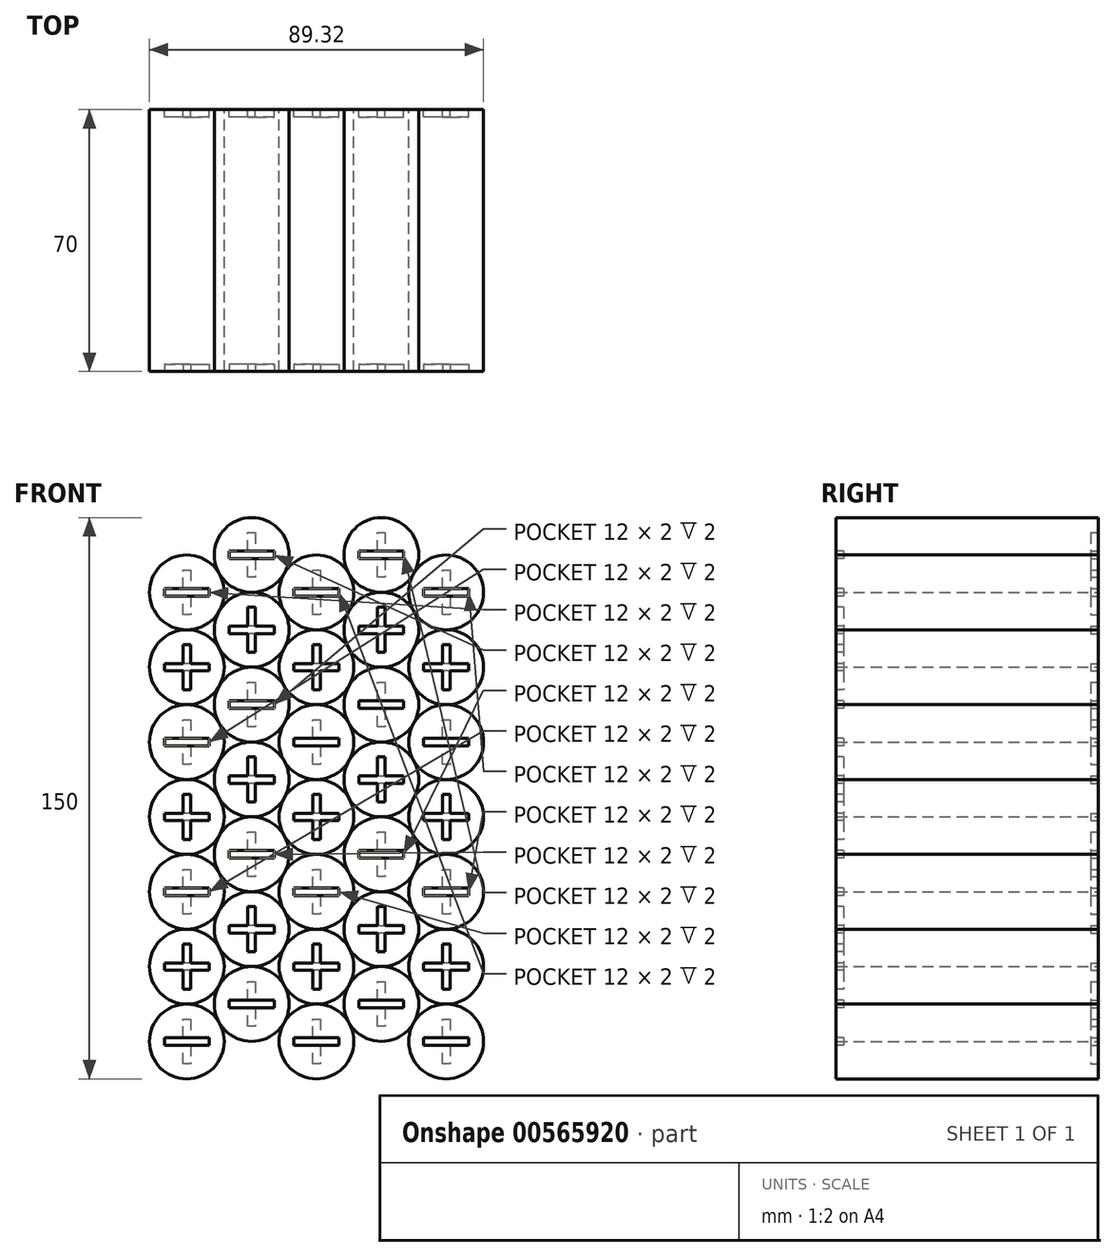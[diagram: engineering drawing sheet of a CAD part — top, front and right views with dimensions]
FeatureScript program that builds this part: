
annotation { "Feature Type Name" : "Feature", "Feature Type Description" : "" }
export const myFeature = defineFeature(function(context is Context, id is Id, definition is map)
    precondition{}
    {
        {
            var Q0;
            Q0=qCreatedBy(makeId("Front.planeOp"),FACE);
            var sketch = newSketch(context, id + "F0", { "sketchPlane" : qUnion([Q0])});
            skCircle(sketch, "E0", {"center": v(10, 10) * mm, "radius": 10 * mm});
            skCircle(sketch, "E1", {"center": v(27.33, 20) * mm, "radius": 10 * mm});
            skCircle(sketch, "E2", {"center": v(44.66, 10) * mm, "radius": 10 * mm});
            skCircle(sketch, "E3", {"center": v(62, 20) * mm, "radius": 10 * mm});
            skCircle(sketch, "E4", {"center": v(79.32, 10) * mm, "radius": 10 * mm});
            skCircle(sketch, "E5", {"center": v(10, 30) * mm, "radius": 10 * mm});
            skCircle(sketch, "E6", {"center": v(27.33, 40) * mm, "radius": 10 * mm});
            skCircle(sketch, "E7", {"center": v(44.66, 30) * mm, "radius": 10 * mm});
            skCircle(sketch, "E8", {"center": v(62, 40) * mm, "radius": 10 * mm});
            skCircle(sketch, "E9", {"center": v(79.32, 30) * mm, "radius": 10 * mm});
            skCircle(sketch, "E10", {"center": v(10, 50) * mm, "radius": 10 * mm});
            skCircle(sketch, "E11", {"center": v(27.33, 60) * mm, "radius": 10 * mm});
            skCircle(sketch, "E12", {"center": v(44.66, 50) * mm, "radius": 10 * mm});
            skCircle(sketch, "E13", {"center": v(62, 60) * mm, "radius": 10 * mm});
            skCircle(sketch, "E14", {"center": v(79.32, 50) * mm, "radius": 10 * mm});
            skCircle(sketch, "E15", {"center": v(10, 70) * mm, "radius": 10 * mm});
            skCircle(sketch, "E16", {"center": v(27.33, 80) * mm, "radius": 10 * mm});
            skCircle(sketch, "E17", {"center": v(44.66, 70) * mm, "radius": 10 * mm});
            skCircle(sketch, "E18", {"center": v(62, 80) * mm, "radius": 10 * mm});
            skCircle(sketch, "E19", {"center": v(79.32, 70) * mm, "radius": 10 * mm});
            skCircle(sketch, "E20", {"center": v(10, 90) * mm, "radius": 10 * mm});
            skCircle(sketch, "E21", {"center": v(27.33, 100) * mm, "radius": 10 * mm});
            skCircle(sketch, "E22", {"center": v(44.66, 90) * mm, "radius": 10 * mm});
            skCircle(sketch, "E23", {"center": v(62, 100) * mm, "radius": 10 * mm});
            skCircle(sketch, "E24", {"center": v(79.32, 90) * mm, "radius": 10 * mm});
            skCircle(sketch, "E25", {"center": v(10, 110) * mm, "radius": 10 * mm});
            skCircle(sketch, "E26", {"center": v(27.33, 120) * mm, "radius": 10 * mm});
            skCircle(sketch, "E27", {"center": v(44.66, 110) * mm, "radius": 10 * mm});
            skCircle(sketch, "E28", {"center": v(62, 120) * mm, "radius": 10 * mm});
            skCircle(sketch, "E29", {"center": v(79.32, 110) * mm, "radius": 10 * mm});
            skCircle(sketch, "E30", {"center": v(10, 130) * mm, "radius": 10 * mm});
            skCircle(sketch, "E31", {"center": v(27.33, 140) * mm, "radius": 10 * mm});
            skCircle(sketch, "E32", {"center": v(44.66, 130) * mm, "radius": 10 * mm});
            skCircle(sketch, "E33", {"center": v(62, 140) * mm, "radius": 10 * mm});
            skCircle(sketch, "E34", {"center": v(79.32, 130) * mm, "radius": 10 * mm});
            skSolve(sketch);
        }
        {
            var Q0;
            Q0=qSketchRegion(id+"F0",true);
            extrude(context, id + "F1", {"entities" : qUnion([Q0]), "depth" : 70 * mm, "offsetDistance" : 25 * mm});
        }
        {
            var Q0;
            Q0=makeQuery(id+"F1.opExtrude","CAP_FACE",FACE,{"disambiguationData":[OSD([sQuery(id+"F0.wireOp",EDGE,"E34")])],"isStart":true});
            var sketch = newSketch(context, id + "F2", { "sketchPlane" : qUnion([Q0])});
            skLineSegment(sketch, "E35", {"start": v(-80.32, 16) * mm, "end": v(-80.32, 11) * mm});
            skLineSegment(sketch, "E36", {"start": v(-80.32, 11) * mm, "end": v(-85.32, 11) * mm});
            skLineSegment(sketch, "E37", {"start": v(-85.32, 11) * mm, "end": v(-85.32, 9) * mm});
            skLineSegment(sketch, "E38", {"start": v(-85.32, 9) * mm, "end": v(-80.32, 9) * mm});
            skLineSegment(sketch, "E39", {"start": v(-80.32, 9) * mm, "end": v(-80.32, 4) * mm});
            skLineSegment(sketch, "E40", {"start": v(-80.32, 4) * mm, "end": v(-78.32, 4) * mm});
            skLineSegment(sketch, "E41", {"start": v(-78.32, 4) * mm, "end": v(-78.32, 9) * mm});
            skLineSegment(sketch, "E42", {"start": v(-78.32, 9) * mm, "end": v(-73.32, 9) * mm});
            skLineSegment(sketch, "E43", {"start": v(-73.32, 9) * mm, "end": v(-73.32, 11) * mm});
            skLineSegment(sketch, "E44", {"start": v(-73.32, 11) * mm, "end": v(-78.32, 11) * mm});
            skLineSegment(sketch, "E45", {"start": v(-78.32, 11) * mm, "end": v(-78.32, 16) * mm});
            skLineSegment(sketch, "E46", {"start": v(-78.32, 16) * mm, "end": v(-80.32, 16) * mm});
            skLineSegment(sketch, "E47", {"start": v(-63, 26) * mm, "end": v(-63, 21) * mm});
            skLineSegment(sketch, "E48", {"start": v(-63, 21) * mm, "end": v(-68, 21) * mm});
            skLineSegment(sketch, "E49", {"start": v(-68, 21) * mm, "end": v(-68, 19) * mm});
            skLineSegment(sketch, "E50", {"start": v(-68, 19) * mm, "end": v(-63, 19) * mm});
            skLineSegment(sketch, "E51", {"start": v(-63, 19) * mm, "end": v(-63, 14) * mm});
            skLineSegment(sketch, "E52", {"start": v(-63, 14) * mm, "end": v(-60.99, 14) * mm});
            skLineSegment(sketch, "E53", {"start": v(-61, 14) * mm, "end": v(-61, 19) * mm});
            skLineSegment(sketch, "E54", {"start": v(-61, 19) * mm, "end": v(-55.99, 19) * mm});
            skLineSegment(sketch, "E55", {"start": v(-55.99, 19) * mm, "end": v(-55.99, 21) * mm});
            skLineSegment(sketch, "E56", {"start": v(-55.99, 21) * mm, "end": v(-61, 21) * mm});
            skLineSegment(sketch, "E57", {"start": v(-61, 21) * mm, "end": v(-61, 26) * mm});
            skLineSegment(sketch, "E58", {"start": v(-61, 26) * mm, "end": v(-63, 26) * mm});
            skLineSegment(sketch, "E59", {"start": v(-11, 16) * mm, "end": v(-11, 11) * mm});
            skLineSegment(sketch, "E60", {"start": v(-11, 11) * mm, "end": v(-16, 11) * mm});
            skLineSegment(sketch, "E61", {"start": v(-16, 11) * mm, "end": v(-16, 9) * mm});
            skLineSegment(sketch, "E62", {"start": v(-16, 9) * mm, "end": v(-11, 9) * mm});
            skLineSegment(sketch, "E63", {"start": v(-11, 9) * mm, "end": v(-11, 4) * mm});
            skLineSegment(sketch, "E64", {"start": v(-11, 4) * mm, "end": v(-9, 4) * mm});
            skLineSegment(sketch, "E65", {"start": v(-9, 4) * mm, "end": v(-9, 9) * mm});
            skLineSegment(sketch, "E66", {"start": v(-9, 9) * mm, "end": v(-4, 9) * mm});
            skLineSegment(sketch, "E67", {"start": v(-4, 9) * mm, "end": v(-4, 11) * mm});
            skLineSegment(sketch, "E68", {"start": v(-4, 11) * mm, "end": v(-9, 11) * mm});
            skLineSegment(sketch, "E69", {"start": v(-9, 11) * mm, "end": v(-9, 16) * mm});
            skLineSegment(sketch, "E70", {"start": v(-9, 16) * mm, "end": v(-11, 16) * mm});
            skLineSegment(sketch, "E71", {"start": v(-28.33, 26) * mm, "end": v(-28.33, 21) * mm});
            skLineSegment(sketch, "E72", {"start": v(-28.33, 21) * mm, "end": v(-33.33, 21) * mm});
            skLineSegment(sketch, "E73", {"start": v(-33.33, 21) * mm, "end": v(-33.33, 19) * mm});
            skLineSegment(sketch, "E74", {"start": v(-33.33, 19) * mm, "end": v(-28.33, 19) * mm});
            skLineSegment(sketch, "E75", {"start": v(-28.33, 19) * mm, "end": v(-28.33, 14) * mm});
            skLineSegment(sketch, "E76", {"start": v(-28.33, 14) * mm, "end": v(-26.33, 14) * mm});
            skLineSegment(sketch, "E77", {"start": v(-26.33, 14) * mm, "end": v(-26.33, 19) * mm});
            skLineSegment(sketch, "E78", {"start": v(-26.33, 19) * mm, "end": v(-21.33, 19) * mm});
            skLineSegment(sketch, "E79", {"start": v(-21.33, 19) * mm, "end": v(-21.33, 21) * mm});
            skLineSegment(sketch, "E80", {"start": v(-21.33, 21) * mm, "end": v(-26.33, 21) * mm});
            skLineSegment(sketch, "E81", {"start": v(-26.33, 21) * mm, "end": v(-26.33, 26) * mm});
            skLineSegment(sketch, "E82", {"start": v(-26.33, 26) * mm, "end": v(-28.33, 26) * mm});
            skLineSegment(sketch, "E83", {"start": v(-45.66, 16) * mm, "end": v(-45.66, 11) * mm});
            skLineSegment(sketch, "E84", {"start": v(-45.66, 11) * mm, "end": v(-50.66, 11) * mm});
            skLineSegment(sketch, "E85", {"start": v(-50.66, 11) * mm, "end": v(-50.66, 9) * mm});
            skLineSegment(sketch, "E86", {"start": v(-50.66, 9) * mm, "end": v(-45.66, 9) * mm});
            skLineSegment(sketch, "E87", {"start": v(-45.66, 9) * mm, "end": v(-45.66, 4) * mm});
            skLineSegment(sketch, "E88", {"start": v(-45.66, 4) * mm, "end": v(-43.66, 4) * mm});
            skLineSegment(sketch, "E89", {"start": v(-43.66, 4) * mm, "end": v(-43.66, 9) * mm});
            skLineSegment(sketch, "E90", {"start": v(-43.66, 9) * mm, "end": v(-38.66, 9) * mm});
            skLineSegment(sketch, "E91", {"start": v(-38.66, 9) * mm, "end": v(-38.66, 11) * mm});
            skLineSegment(sketch, "E92", {"start": v(-38.66, 11) * mm, "end": v(-43.66, 11) * mm});
            skLineSegment(sketch, "E93", {"start": v(-43.66, 11) * mm, "end": v(-43.66, 16) * mm});
            skLineSegment(sketch, "E94", {"start": v(-43.66, 16) * mm, "end": v(-45.66, 16) * mm});
            skLineSegment(sketch, "E95.bottom", {"start": v(-85.32, 31) * mm, "end": v(-73.32, 31) * mm});
            skLineSegment(sketch, "E95.top", {"start": v(-85.32, 29) * mm, "end": v(-73.32, 29) * mm});
            skLineSegment(sketch, "E95.left", {"start": v(-85.32, 31) * mm, "end": v(-85.32, 29) * mm});
            skLineSegment(sketch, "E95.right", {"start": v(-73.32, 31) * mm, "end": v(-73.32, 29) * mm});
            skLineSegment(sketch, "E96.bottom", {"start": v(-55.99, 41) * mm, "end": v(-68, 41) * mm});
            skLineSegment(sketch, "E96.top", {"start": v(-68, 39) * mm, "end": v(-55.99, 39) * mm});
            skLineSegment(sketch, "E96.left", {"start": v(-68, 41) * mm, "end": v(-68, 39) * mm});
            skLineSegment(sketch, "E96.right", {"start": v(-55.99, 41) * mm, "end": v(-55.99, 39) * mm});
            skLineSegment(sketch, "E97.bottom", {"start": v(-50.66, 31) * mm, "end": v(-38.66, 31) * mm});
            skLineSegment(sketch, "E97.top", {"start": v(-50.66, 29) * mm, "end": v(-38.66, 29) * mm});
            skLineSegment(sketch, "E97.left", {"start": v(-50.66, 31) * mm, "end": v(-50.66, 29) * mm});
            skLineSegment(sketch, "E97.right", {"start": v(-38.66, 31) * mm, "end": v(-38.66, 29) * mm});
            skLineSegment(sketch, "E98.bottom", {"start": v(-33.33, 41) * mm, "end": v(-21.33, 41) * mm});
            skLineSegment(sketch, "E98.top", {"start": v(-33.33, 39) * mm, "end": v(-21.33, 39) * mm});
            skLineSegment(sketch, "E98.left", {"start": v(-33.33, 41) * mm, "end": v(-33.33, 39) * mm});
            skLineSegment(sketch, "E98.right", {"start": v(-21.33, 41) * mm, "end": v(-21.33, 39) * mm});
            skLineSegment(sketch, "E99.bottom", {"start": v(-16, 31) * mm, "end": v(-4, 31) * mm});
            skLineSegment(sketch, "E99.top", {"start": v(-16, 29) * mm, "end": v(-4, 29) * mm});
            skLineSegment(sketch, "E99.left", {"start": v(-16, 31) * mm, "end": v(-16, 29) * mm});
            skLineSegment(sketch, "E99.right", {"start": v(-4, 31) * mm, "end": v(-4, 29) * mm});
            skLineSegment(sketch, "E100", {"start": v(-80.32, 56) * mm, "end": v(-80.32, 51) * mm});
            skLineSegment(sketch, "E101", {"start": v(-80.32, 51) * mm, "end": v(-85.32, 51) * mm});
            skLineSegment(sketch, "E102", {"start": v(-85.32, 51) * mm, "end": v(-85.32, 49) * mm});
            skLineSegment(sketch, "E103", {"start": v(-85.32, 49) * mm, "end": v(-80.32, 49) * mm});
            skLineSegment(sketch, "E104", {"start": v(-80.32, 49) * mm, "end": v(-80.32, 44) * mm});
            skLineSegment(sketch, "E105", {"start": v(-80.32, 44) * mm, "end": v(-78.32, 44) * mm});
            skLineSegment(sketch, "E106", {"start": v(-78.32, 44) * mm, "end": v(-78.32, 49) * mm});
            skLineSegment(sketch, "E107", {"start": v(-78.32, 49) * mm, "end": v(-73.32, 49) * mm});
            skLineSegment(sketch, "E108", {"start": v(-73.32, 49) * mm, "end": v(-73.32, 51) * mm});
            skLineSegment(sketch, "E109", {"start": v(-73.32, 51) * mm, "end": v(-78.32, 51) * mm});
            skLineSegment(sketch, "E110", {"start": v(-78.32, 51) * mm, "end": v(-78.32, 56) * mm});
            skLineSegment(sketch, "E111", {"start": v(-78.32, 56) * mm, "end": v(-80.32, 56) * mm});
            skLineSegment(sketch, "E112", {"start": v(-63, 66) * mm, "end": v(-63, 61) * mm});
            skLineSegment(sketch, "E113", {"start": v(-63, 61) * mm, "end": v(-68, 61) * mm});
            skLineSegment(sketch, "E114", {"start": v(-68, 61) * mm, "end": v(-68, 59) * mm});
            skLineSegment(sketch, "E115", {"start": v(-68, 59) * mm, "end": v(-63, 59) * mm});
            skLineSegment(sketch, "E116", {"start": v(-63, 59) * mm, "end": v(-63, 54) * mm});
            skLineSegment(sketch, "E117", {"start": v(-63, 54) * mm, "end": v(-61, 54) * mm});
            skLineSegment(sketch, "E118", {"start": v(-61, 54) * mm, "end": v(-61, 59) * mm});
            skLineSegment(sketch, "E119", {"start": v(-61, 59) * mm, "end": v(-55.99, 59) * mm});
            skLineSegment(sketch, "E120", {"start": v(-55.99, 59) * mm, "end": v(-55.99, 61) * mm});
            skLineSegment(sketch, "E121", {"start": v(-55.99, 61) * mm, "end": v(-61, 61) * mm});
            skLineSegment(sketch, "E122", {"start": v(-61, 61) * mm, "end": v(-61, 66) * mm});
            skLineSegment(sketch, "E123", {"start": v(-61, 66) * mm, "end": v(-62.99, 66) * mm});
            skLineSegment(sketch, "E124", {"start": v(-11, 56) * mm, "end": v(-11, 51) * mm});
            skLineSegment(sketch, "E125", {"start": v(-11, 51) * mm, "end": v(-16, 51) * mm});
            skLineSegment(sketch, "E126", {"start": v(-16, 51) * mm, "end": v(-16, 49) * mm});
            skLineSegment(sketch, "E127", {"start": v(-16, 49) * mm, "end": v(-11, 49) * mm});
            skLineSegment(sketch, "E128", {"start": v(-11, 49) * mm, "end": v(-11, 44) * mm});
            skLineSegment(sketch, "E129", {"start": v(-11, 44) * mm, "end": v(-9, 44) * mm});
            skLineSegment(sketch, "E130", {"start": v(-9, 44) * mm, "end": v(-9, 49) * mm});
            skLineSegment(sketch, "E131", {"start": v(-9, 49) * mm, "end": v(-4, 49) * mm});
            skLineSegment(sketch, "E132", {"start": v(-4, 49) * mm, "end": v(-4, 51) * mm});
            skLineSegment(sketch, "E133", {"start": v(-4, 51) * mm, "end": v(-9, 51) * mm});
            skLineSegment(sketch, "E134", {"start": v(-9, 51) * mm, "end": v(-9, 56) * mm});
            skLineSegment(sketch, "E135", {"start": v(-9, 56) * mm, "end": v(-11, 56) * mm});
            skLineSegment(sketch, "E136", {"start": v(-28.33, 66) * mm, "end": v(-28.33, 61) * mm});
            skLineSegment(sketch, "E137", {"start": v(-28.33, 61) * mm, "end": v(-33.33, 61) * mm});
            skLineSegment(sketch, "E138", {"start": v(-33.33, 61) * mm, "end": v(-33.33, 59) * mm});
            skLineSegment(sketch, "E139", {"start": v(-33.33, 59) * mm, "end": v(-28.33, 59) * mm});
            skLineSegment(sketch, "E140", {"start": v(-28.33, 59) * mm, "end": v(-28.33, 54) * mm});
            skLineSegment(sketch, "E141", {"start": v(-28.33, 54) * mm, "end": v(-26.33, 54) * mm});
            skLineSegment(sketch, "E142", {"start": v(-26.33, 54) * mm, "end": v(-26.33, 59) * mm});
            skLineSegment(sketch, "E143", {"start": v(-26.33, 59) * mm, "end": v(-21.33, 59) * mm});
            skLineSegment(sketch, "E144", {"start": v(-21.33, 59) * mm, "end": v(-21.33, 61) * mm});
            skLineSegment(sketch, "E145", {"start": v(-21.33, 61) * mm, "end": v(-26.33, 61) * mm});
            skLineSegment(sketch, "E146", {"start": v(-26.33, 61) * mm, "end": v(-26.33, 66) * mm});
            skLineSegment(sketch, "E147", {"start": v(-26.33, 66) * mm, "end": v(-28.33, 66) * mm});
            skLineSegment(sketch, "E148", {"start": v(-45.66, 56) * mm, "end": v(-45.66, 51) * mm});
            skLineSegment(sketch, "E149", {"start": v(-45.66, 51) * mm, "end": v(-50.66, 51) * mm});
            skLineSegment(sketch, "E150", {"start": v(-50.66, 51) * mm, "end": v(-50.66, 49) * mm});
            skLineSegment(sketch, "E151", {"start": v(-50.66, 49) * mm, "end": v(-45.66, 49) * mm});
            skLineSegment(sketch, "E152", {"start": v(-45.66, 49) * mm, "end": v(-45.66, 44) * mm});
            skLineSegment(sketch, "E153", {"start": v(-45.66, 44) * mm, "end": v(-43.66, 44) * mm});
            skLineSegment(sketch, "E154", {"start": v(-43.66, 44) * mm, "end": v(-43.66, 49) * mm});
            skLineSegment(sketch, "E155", {"start": v(-43.66, 49) * mm, "end": v(-38.66, 49) * mm});
            skLineSegment(sketch, "E156", {"start": v(-38.66, 49) * mm, "end": v(-38.66, 51) * mm});
            skLineSegment(sketch, "E157", {"start": v(-38.66, 51) * mm, "end": v(-43.66, 51) * mm});
            skLineSegment(sketch, "E158", {"start": v(-43.66, 51) * mm, "end": v(-43.66, 56) * mm});
            skLineSegment(sketch, "E159", {"start": v(-43.66, 56) * mm, "end": v(-45.66, 56) * mm});
            skLineSegment(sketch, "E160.bottom", {"start": v(-85.32, 71) * mm, "end": v(-73.32, 71) * mm});
            skLineSegment(sketch, "E160.top", {"start": v(-85.32, 69) * mm, "end": v(-73.32, 69) * mm});
            skLineSegment(sketch, "E160.left", {"start": v(-85.32, 71) * mm, "end": v(-85.32, 69) * mm});
            skLineSegment(sketch, "E160.right", {"start": v(-73.32, 71) * mm, "end": v(-73.32, 69) * mm});
            skLineSegment(sketch, "E161.bottom", {"start": v(-55.99, 81) * mm, "end": v(-68, 81) * mm});
            skLineSegment(sketch, "E161.top", {"start": v(-68, 79) * mm, "end": v(-55.99, 79) * mm});
            skLineSegment(sketch, "E161.left", {"start": v(-68, 81) * mm, "end": v(-68, 79) * mm});
            skLineSegment(sketch, "E161.right", {"start": v(-55.99, 81) * mm, "end": v(-55.99, 79) * mm});
            skLineSegment(sketch, "E162.bottom", {"start": v(-50.66, 71) * mm, "end": v(-38.66, 71) * mm});
            skLineSegment(sketch, "E162.top", {"start": v(-50.66, 69) * mm, "end": v(-38.66, 69) * mm});
            skLineSegment(sketch, "E162.left", {"start": v(-50.66, 71) * mm, "end": v(-50.66, 69) * mm});
            skLineSegment(sketch, "E162.right", {"start": v(-38.66, 71) * mm, "end": v(-38.66, 69) * mm});
            skLineSegment(sketch, "E163.bottom", {"start": v(-33.33, 81) * mm, "end": v(-21.33, 81) * mm});
            skLineSegment(sketch, "E163.top", {"start": v(-33.33, 79) * mm, "end": v(-21.33, 79) * mm});
            skLineSegment(sketch, "E163.left", {"start": v(-33.33, 81) * mm, "end": v(-33.33, 79) * mm});
            skLineSegment(sketch, "E163.right", {"start": v(-21.33, 81) * mm, "end": v(-21.33, 79) * mm});
            skLineSegment(sketch, "E164.bottom", {"start": v(-16, 71) * mm, "end": v(-4, 71) * mm});
            skLineSegment(sketch, "E164.top", {"start": v(-16, 69) * mm, "end": v(-4, 69) * mm});
            skLineSegment(sketch, "E164.left", {"start": v(-16, 71) * mm, "end": v(-16, 69) * mm});
            skLineSegment(sketch, "E164.right", {"start": v(-4, 71) * mm, "end": v(-4, 69) * mm});
            skLineSegment(sketch, "E165", {"start": v(-80.32, 96) * mm, "end": v(-80.32, 91) * mm});
            skLineSegment(sketch, "E166", {"start": v(-80.32, 91) * mm, "end": v(-85.32, 91) * mm});
            skLineSegment(sketch, "E167", {"start": v(-85.32, 91) * mm, "end": v(-85.32, 89) * mm});
            skLineSegment(sketch, "E168", {"start": v(-85.32, 89) * mm, "end": v(-80.32, 89) * mm});
            skLineSegment(sketch, "E169", {"start": v(-80.32, 89) * mm, "end": v(-80.32, 84) * mm});
            skLineSegment(sketch, "E170", {"start": v(-80.32, 84) * mm, "end": v(-78.32, 84) * mm});
            skLineSegment(sketch, "E171", {"start": v(-78.32, 84) * mm, "end": v(-78.32, 89) * mm});
            skLineSegment(sketch, "E172", {"start": v(-78.32, 89) * mm, "end": v(-73.32, 89) * mm});
            skLineSegment(sketch, "E173", {"start": v(-73.32, 89) * mm, "end": v(-73.32, 91) * mm});
            skLineSegment(sketch, "E174", {"start": v(-73.32, 91) * mm, "end": v(-78.32, 91) * mm});
            skLineSegment(sketch, "E175", {"start": v(-78.32, 91) * mm, "end": v(-78.32, 96) * mm});
            skLineSegment(sketch, "E176", {"start": v(-78.32, 96) * mm, "end": v(-80.32, 96) * mm});
            skLineSegment(sketch, "E177", {"start": v(-63, 106) * mm, "end": v(-63, 101) * mm});
            skLineSegment(sketch, "E178", {"start": v(-63, 101) * mm, "end": v(-68, 101) * mm});
            skLineSegment(sketch, "E179", {"start": v(-68, 101) * mm, "end": v(-68, 99) * mm});
            skLineSegment(sketch, "E180", {"start": v(-68, 99) * mm, "end": v(-63, 99) * mm});
            skLineSegment(sketch, "E181", {"start": v(-63, 99) * mm, "end": v(-63, 94) * mm});
            skLineSegment(sketch, "E182", {"start": v(-63, 94) * mm, "end": v(-61, 94) * mm});
            skLineSegment(sketch, "E183", {"start": v(-61, 94) * mm, "end": v(-61, 99) * mm});
            skLineSegment(sketch, "E184", {"start": v(-61, 99) * mm, "end": v(-56, 99) * mm});
            skLineSegment(sketch, "E185", {"start": v(-56, 99) * mm, "end": v(-56, 101) * mm});
            skLineSegment(sketch, "E186", {"start": v(-56, 101) * mm, "end": v(-61, 101) * mm});
            skLineSegment(sketch, "E187", {"start": v(-61, 101) * mm, "end": v(-61, 106) * mm});
            skLineSegment(sketch, "E188", {"start": v(-61, 106) * mm, "end": v(-62.99, 106) * mm});
            skLineSegment(sketch, "E189", {"start": v(-11, 96) * mm, "end": v(-11, 91) * mm});
            skLineSegment(sketch, "E190", {"start": v(-11, 91) * mm, "end": v(-16, 91) * mm});
            skLineSegment(sketch, "E191", {"start": v(-16, 91) * mm, "end": v(-16, 89) * mm});
            skLineSegment(sketch, "E192", {"start": v(-16, 89) * mm, "end": v(-11, 89) * mm});
            skLineSegment(sketch, "E193", {"start": v(-11, 89) * mm, "end": v(-11, 84) * mm});
            skLineSegment(sketch, "E194", {"start": v(-11, 84) * mm, "end": v(-9, 84) * mm});
            skLineSegment(sketch, "E195", {"start": v(-9, 84) * mm, "end": v(-9, 89) * mm});
            skLineSegment(sketch, "E196", {"start": v(-9, 89) * mm, "end": v(-4, 89) * mm});
            skLineSegment(sketch, "E197", {"start": v(-4, 89) * mm, "end": v(-4, 91) * mm});
            skLineSegment(sketch, "E198", {"start": v(-4, 91) * mm, "end": v(-9, 91) * mm});
            skLineSegment(sketch, "E199", {"start": v(-9, 91) * mm, "end": v(-9, 96) * mm});
            skLineSegment(sketch, "E200", {"start": v(-9, 96) * mm, "end": v(-11, 96) * mm});
            skLineSegment(sketch, "E201", {"start": v(-28.33, 106) * mm, "end": v(-28.33, 101) * mm});
            skLineSegment(sketch, "E202", {"start": v(-28.33, 101) * mm, "end": v(-33.33, 101) * mm});
            skLineSegment(sketch, "E203", {"start": v(-33.33, 101) * mm, "end": v(-33.33, 99) * mm});
            skLineSegment(sketch, "E204", {"start": v(-33.33, 99) * mm, "end": v(-28.33, 99) * mm});
            skLineSegment(sketch, "E205", {"start": v(-28.33, 99) * mm, "end": v(-28.33, 94) * mm});
            skLineSegment(sketch, "E206", {"start": v(-28.33, 94) * mm, "end": v(-26.33, 94) * mm});
            skLineSegment(sketch, "E207", {"start": v(-26.33, 94) * mm, "end": v(-26.33, 99) * mm});
            skLineSegment(sketch, "E208", {"start": v(-26.33, 99) * mm, "end": v(-21.33, 99) * mm});
            skLineSegment(sketch, "E209", {"start": v(-21.33, 99) * mm, "end": v(-21.33, 101) * mm});
            skLineSegment(sketch, "E210", {"start": v(-21.33, 101) * mm, "end": v(-26.33, 101) * mm});
            skLineSegment(sketch, "E211", {"start": v(-26.33, 101) * mm, "end": v(-26.33, 106) * mm});
            skLineSegment(sketch, "E212", {"start": v(-26.33, 106) * mm, "end": v(-28.33, 106) * mm});
            skLineSegment(sketch, "E213", {"start": v(-45.66, 96) * mm, "end": v(-45.66, 91) * mm});
            skLineSegment(sketch, "E214", {"start": v(-45.66, 91) * mm, "end": v(-50.66, 91) * mm});
            skLineSegment(sketch, "E215", {"start": v(-50.66, 91) * mm, "end": v(-50.66, 89) * mm});
            skLineSegment(sketch, "E216", {"start": v(-50.66, 89) * mm, "end": v(-45.66, 89) * mm});
            skLineSegment(sketch, "E217", {"start": v(-45.66, 89) * mm, "end": v(-45.66, 84) * mm});
            skLineSegment(sketch, "E218", {"start": v(-45.66, 84) * mm, "end": v(-43.66, 84) * mm});
            skLineSegment(sketch, "E219", {"start": v(-43.66, 84) * mm, "end": v(-43.66, 89) * mm});
            skLineSegment(sketch, "E220", {"start": v(-43.66, 89) * mm, "end": v(-38.66, 89) * mm});
            skLineSegment(sketch, "E221", {"start": v(-38.66, 89) * mm, "end": v(-38.66, 91) * mm});
            skLineSegment(sketch, "E222", {"start": v(-38.66, 91) * mm, "end": v(-43.66, 91) * mm});
            skLineSegment(sketch, "E223", {"start": v(-43.66, 91) * mm, "end": v(-43.66, 96) * mm});
            skLineSegment(sketch, "E224", {"start": v(-43.66, 96) * mm, "end": v(-45.66, 96) * mm});
            skLineSegment(sketch, "E225.bottom", {"start": v(-85.32, 111) * mm, "end": v(-73.32, 111) * mm});
            skLineSegment(sketch, "E225.top", {"start": v(-85.32, 109) * mm, "end": v(-73.32, 109) * mm});
            skLineSegment(sketch, "E225.left", {"start": v(-85.32, 111) * mm, "end": v(-85.32, 109) * mm});
            skLineSegment(sketch, "E225.right", {"start": v(-73.32, 111) * mm, "end": v(-73.32, 109) * mm});
            skLineSegment(sketch, "E226.bottom", {"start": v(-55.99, 121) * mm, "end": v(-68, 121) * mm});
            skLineSegment(sketch, "E226.top", {"start": v(-68, 119) * mm, "end": v(-55.99, 119) * mm});
            skLineSegment(sketch, "E226.left", {"start": v(-68, 121) * mm, "end": v(-68, 119) * mm});
            skLineSegment(sketch, "E226.right", {"start": v(-55.99, 121) * mm, "end": v(-55.99, 119) * mm});
            skLineSegment(sketch, "E227.bottom", {"start": v(-50.66, 111) * mm, "end": v(-38.66, 111) * mm});
            skLineSegment(sketch, "E227.top", {"start": v(-50.66, 109) * mm, "end": v(-38.66, 109) * mm});
            skLineSegment(sketch, "E227.left", {"start": v(-50.66, 111) * mm, "end": v(-50.66, 109) * mm});
            skLineSegment(sketch, "E227.right", {"start": v(-38.66, 111) * mm, "end": v(-38.66, 109) * mm});
            skLineSegment(sketch, "E228.bottom", {"start": v(-33.33, 121) * mm, "end": v(-21.33, 121) * mm});
            skLineSegment(sketch, "E228.top", {"start": v(-33.33, 119) * mm, "end": v(-21.33, 119) * mm});
            skLineSegment(sketch, "E228.left", {"start": v(-33.33, 121) * mm, "end": v(-33.33, 119) * mm});
            skLineSegment(sketch, "E228.right", {"start": v(-21.33, 121) * mm, "end": v(-21.33, 119) * mm});
            skLineSegment(sketch, "E229.bottom", {"start": v(-16, 111) * mm, "end": v(-4, 111) * mm});
            skLineSegment(sketch, "E229.top", {"start": v(-16, 109) * mm, "end": v(-4, 109) * mm});
            skLineSegment(sketch, "E229.left", {"start": v(-16, 111) * mm, "end": v(-16, 109) * mm});
            skLineSegment(sketch, "E229.right", {"start": v(-4, 111) * mm, "end": v(-4, 109) * mm});
            skLineSegment(sketch, "E230", {"start": v(-80.32, 136) * mm, "end": v(-80.32, 131) * mm});
            skLineSegment(sketch, "E231", {"start": v(-80.32, 131) * mm, "end": v(-85.32, 131) * mm});
            skLineSegment(sketch, "E232", {"start": v(-85.32, 131) * mm, "end": v(-85.32, 129) * mm});
            skLineSegment(sketch, "E233", {"start": v(-85.32, 129) * mm, "end": v(-80.32, 129) * mm});
            skLineSegment(sketch, "E234", {"start": v(-80.32, 129) * mm, "end": v(-80.32, 124) * mm});
            skLineSegment(sketch, "E235", {"start": v(-80.32, 124) * mm, "end": v(-78.32, 124) * mm});
            skLineSegment(sketch, "E236", {"start": v(-78.32, 124) * mm, "end": v(-78.32, 129) * mm});
            skLineSegment(sketch, "E237", {"start": v(-78.32, 129) * mm, "end": v(-73.32, 129) * mm});
            skLineSegment(sketch, "E238", {"start": v(-73.32, 129) * mm, "end": v(-73.32, 131) * mm});
            skLineSegment(sketch, "E239", {"start": v(-73.32, 131) * mm, "end": v(-78.32, 131) * mm});
            skLineSegment(sketch, "E240", {"start": v(-78.32, 131) * mm, "end": v(-78.32, 136) * mm});
            skLineSegment(sketch, "E241", {"start": v(-78.32, 136) * mm, "end": v(-80.32, 136) * mm});
            skLineSegment(sketch, "E242", {"start": v(-62.99, 146) * mm, "end": v(-62.99, 141) * mm});
            skLineSegment(sketch, "E243", {"start": v(-62.99, 141) * mm, "end": v(-67.99, 141) * mm});
            skLineSegment(sketch, "E244", {"start": v(-67.99, 141) * mm, "end": v(-67.99, 139) * mm});
            skLineSegment(sketch, "E245", {"start": v(-67.99, 139) * mm, "end": v(-62.99, 139) * mm});
            skLineSegment(sketch, "E246", {"start": v(-62.99, 139) * mm, "end": v(-62.99, 134) * mm});
            skLineSegment(sketch, "E247", {"start": v(-62.99, 134) * mm, "end": v(-60.99, 134) * mm});
            skLineSegment(sketch, "E248", {"start": v(-60.99, 134) * mm, "end": v(-60.99, 139) * mm});
            skLineSegment(sketch, "E249", {"start": v(-60.99, 139) * mm, "end": v(-55.99, 139) * mm});
            skLineSegment(sketch, "E250", {"start": v(-55.99, 139) * mm, "end": v(-55.99, 141) * mm});
            skLineSegment(sketch, "E251", {"start": v(-55.99, 141) * mm, "end": v(-60.99, 141) * mm});
            skLineSegment(sketch, "E252", {"start": v(-60.99, 141) * mm, "end": v(-60.99, 146) * mm});
            skLineSegment(sketch, "E253", {"start": v(-60.99, 146) * mm, "end": v(-62.99, 146) * mm});
            skLineSegment(sketch, "E254", {"start": v(-11, 136) * mm, "end": v(-11, 131) * mm});
            skLineSegment(sketch, "E255", {"start": v(-11, 131) * mm, "end": v(-16, 131) * mm});
            skLineSegment(sketch, "E256", {"start": v(-16, 131) * mm, "end": v(-16, 129) * mm});
            skLineSegment(sketch, "E257", {"start": v(-16, 129) * mm, "end": v(-11, 129) * mm});
            skLineSegment(sketch, "E258", {"start": v(-11, 129) * mm, "end": v(-11, 124) * mm});
            skLineSegment(sketch, "E259", {"start": v(-11, 124) * mm, "end": v(-9, 124) * mm});
            skLineSegment(sketch, "E260", {"start": v(-9, 124) * mm, "end": v(-9, 129) * mm});
            skLineSegment(sketch, "E261", {"start": v(-9, 129) * mm, "end": v(-4, 129) * mm});
            skLineSegment(sketch, "E262", {"start": v(-4, 129) * mm, "end": v(-4, 131) * mm});
            skLineSegment(sketch, "E263", {"start": v(-4, 131) * mm, "end": v(-9, 131) * mm});
            skLineSegment(sketch, "E264", {"start": v(-9, 131) * mm, "end": v(-9, 136) * mm});
            skLineSegment(sketch, "E265", {"start": v(-9, 136) * mm, "end": v(-11, 136) * mm});
            skLineSegment(sketch, "E266", {"start": v(-28.33, 146) * mm, "end": v(-28.33, 141) * mm});
            skLineSegment(sketch, "E267", {"start": v(-28.33, 141) * mm, "end": v(-33.33, 141) * mm});
            skLineSegment(sketch, "E268", {"start": v(-33.33, 141) * mm, "end": v(-33.33, 139) * mm});
            skLineSegment(sketch, "E269", {"start": v(-33.33, 139) * mm, "end": v(-28.33, 139) * mm});
            skLineSegment(sketch, "E270", {"start": v(-28.33, 139) * mm, "end": v(-28.33, 134) * mm});
            skLineSegment(sketch, "E271", {"start": v(-28.33, 134) * mm, "end": v(-26.33, 134) * mm});
            skLineSegment(sketch, "E272", {"start": v(-26.33, 134) * mm, "end": v(-26.33, 139) * mm});
            skLineSegment(sketch, "E273", {"start": v(-26.33, 139) * mm, "end": v(-21.33, 139) * mm});
            skLineSegment(sketch, "E274", {"start": v(-21.33, 139) * mm, "end": v(-21.33, 141) * mm});
            skLineSegment(sketch, "E275", {"start": v(-21.33, 141) * mm, "end": v(-26.33, 141) * mm});
            skLineSegment(sketch, "E276", {"start": v(-26.33, 141) * mm, "end": v(-26.33, 146) * mm});
            skLineSegment(sketch, "E277", {"start": v(-26.33, 146) * mm, "end": v(-28.33, 146) * mm});
            skLineSegment(sketch, "E278", {"start": v(-45.66, 136) * mm, "end": v(-45.66, 131) * mm});
            skLineSegment(sketch, "E279", {"start": v(-45.66, 131) * mm, "end": v(-50.66, 131) * mm});
            skLineSegment(sketch, "E280", {"start": v(-50.66, 131) * mm, "end": v(-50.66, 129) * mm});
            skLineSegment(sketch, "E281", {"start": v(-50.66, 129) * mm, "end": v(-45.66, 129) * mm});
            skLineSegment(sketch, "E282", {"start": v(-45.66, 129) * mm, "end": v(-45.66, 124) * mm});
            skLineSegment(sketch, "E283", {"start": v(-45.66, 124) * mm, "end": v(-43.66, 124) * mm});
            skLineSegment(sketch, "E284", {"start": v(-43.66, 124) * mm, "end": v(-43.66, 129) * mm});
            skLineSegment(sketch, "E285", {"start": v(-43.66, 129) * mm, "end": v(-38.66, 129) * mm});
            skLineSegment(sketch, "E286", {"start": v(-38.66, 129) * mm, "end": v(-38.66, 131) * mm});
            skLineSegment(sketch, "E287", {"start": v(-38.66, 131) * mm, "end": v(-43.66, 131) * mm});
            skLineSegment(sketch, "E288", {"start": v(-43.66, 131) * mm, "end": v(-43.66, 136) * mm});
            skLineSegment(sketch, "E289", {"start": v(-43.66, 136) * mm, "end": v(-45.66, 136) * mm});
            skSolve(sketch);
        }
        {
            var Q0;
            Q0=qSketchRegion(id+"F2",true);
            extrude(context, id + "F3", {"entities" : qUnion([Q0]), "operationType" : NewBodyOperationType.REMOVE, "oppositeDirection" : true, "depth" : 2 * mm, "offsetDistance" : 25 * mm});
        }
        {
            var Q0;
            Q0=makeQuery(id+"F1.opExtrude","CAP_FACE",FACE,{"disambiguationData":[OSD([sQuery(id+"F0.wireOp",EDGE,"E25")])],"isStart":false});
            var sketch = newSketch(context, id + "F4", { "sketchPlane" : qUnion([Q0])});
            skLineSegment(sketch, "E290", {"start": v(9, 36) * mm, "end": v(9, 31) * mm});
            skLineSegment(sketch, "E291", {"start": v(9, 31) * mm, "end": v(4, 31) * mm});
            skLineSegment(sketch, "E292", {"start": v(4, 31) * mm, "end": v(4, 29) * mm});
            skLineSegment(sketch, "E293", {"start": v(4, 29) * mm, "end": v(9, 29) * mm});
            skLineSegment(sketch, "E294", {"start": v(9, 29) * mm, "end": v(9, 24) * mm});
            skLineSegment(sketch, "E295", {"start": v(9, 24) * mm, "end": v(11, 24) * mm});
            skLineSegment(sketch, "E296", {"start": v(11, 24) * mm, "end": v(11, 29) * mm});
            skLineSegment(sketch, "E297", {"start": v(11, 29) * mm, "end": v(16, 29) * mm});
            skLineSegment(sketch, "E298", {"start": v(16, 29) * mm, "end": v(16, 31) * mm});
            skLineSegment(sketch, "E299", {"start": v(16, 31) * mm, "end": v(11, 31) * mm});
            skLineSegment(sketch, "E300", {"start": v(11, 31) * mm, "end": v(11, 36) * mm});
            skLineSegment(sketch, "E301", {"start": v(11, 36) * mm, "end": v(9, 36) * mm});
            skLineSegment(sketch, "E302", {"start": v(26.33, 46) * mm, "end": v(26.33, 41) * mm});
            skLineSegment(sketch, "E303", {"start": v(26.33, 41) * mm, "end": v(21.33, 41) * mm});
            skLineSegment(sketch, "E304", {"start": v(21.33, 41) * mm, "end": v(21.33, 39) * mm});
            skLineSegment(sketch, "E305", {"start": v(21.33, 39) * mm, "end": v(26.33, 39) * mm});
            skLineSegment(sketch, "E306", {"start": v(26.33, 39) * mm, "end": v(26.33, 34) * mm});
            skLineSegment(sketch, "E307", {"start": v(26.33, 34) * mm, "end": v(28.33, 34) * mm});
            skLineSegment(sketch, "E308", {"start": v(28.33, 34) * mm, "end": v(28.33, 39) * mm});
            skLineSegment(sketch, "E309", {"start": v(28.33, 39) * mm, "end": v(33.33, 39) * mm});
            skLineSegment(sketch, "E310", {"start": v(33.33, 39) * mm, "end": v(33.33, 41) * mm});
            skLineSegment(sketch, "E311", {"start": v(33.33, 41) * mm, "end": v(28.33, 41) * mm});
            skLineSegment(sketch, "E312", {"start": v(28.33, 41) * mm, "end": v(28.33, 46) * mm});
            skLineSegment(sketch, "E313", {"start": v(28.33, 46) * mm, "end": v(26.33, 46) * mm});
            skLineSegment(sketch, "E314", {"start": v(78.32, 36) * mm, "end": v(78.32, 31) * mm});
            skLineSegment(sketch, "E315", {"start": v(78.32, 31) * mm, "end": v(73.32, 31) * mm});
            skLineSegment(sketch, "E316", {"start": v(73.32, 31) * mm, "end": v(73.32, 29) * mm});
            skLineSegment(sketch, "E317", {"start": v(73.32, 29) * mm, "end": v(78.32, 29) * mm});
            skLineSegment(sketch, "E318", {"start": v(78.32, 29) * mm, "end": v(78.32, 24) * mm});
            skLineSegment(sketch, "E319", {"start": v(78.32, 24) * mm, "end": v(80.32, 24) * mm});
            skLineSegment(sketch, "E320", {"start": v(80.32, 24) * mm, "end": v(80.32, 29) * mm});
            skLineSegment(sketch, "E321", {"start": v(80.32, 29) * mm, "end": v(85.32, 29) * mm});
            skLineSegment(sketch, "E322", {"start": v(85.32, 29) * mm, "end": v(85.32, 31) * mm});
            skLineSegment(sketch, "E323", {"start": v(85.32, 31) * mm, "end": v(80.32, 31) * mm});
            skLineSegment(sketch, "E324", {"start": v(80.32, 31) * mm, "end": v(80.32, 36) * mm});
            skLineSegment(sketch, "E325", {"start": v(80.32, 36) * mm, "end": v(78.32, 36) * mm});
            skLineSegment(sketch, "E326", {"start": v(61, 46) * mm, "end": v(61, 41) * mm});
            skLineSegment(sketch, "E327", {"start": v(61, 41) * mm, "end": v(56, 41) * mm});
            skLineSegment(sketch, "E328", {"start": v(56, 41) * mm, "end": v(56, 39) * mm});
            skLineSegment(sketch, "E329", {"start": v(56, 39) * mm, "end": v(61, 39) * mm});
            skLineSegment(sketch, "E330", {"start": v(61, 39) * mm, "end": v(61, 34) * mm});
            skLineSegment(sketch, "E331", {"start": v(61, 34) * mm, "end": v(63, 34) * mm});
            skLineSegment(sketch, "E332", {"start": v(63, 34) * mm, "end": v(63, 39) * mm});
            skLineSegment(sketch, "E333", {"start": v(63, 39) * mm, "end": v(68, 39) * mm});
            skLineSegment(sketch, "E334", {"start": v(68, 39) * mm, "end": v(68, 41) * mm});
            skLineSegment(sketch, "E335", {"start": v(67.99, 41) * mm, "end": v(63, 41) * mm});
            skLineSegment(sketch, "E336", {"start": v(63, 41) * mm, "end": v(63, 46) * mm});
            skLineSegment(sketch, "E337", {"start": v(63, 46) * mm, "end": v(61, 46) * mm});
            skLineSegment(sketch, "E338", {"start": v(43.66, 36) * mm, "end": v(43.66, 31) * mm});
            skLineSegment(sketch, "E339", {"start": v(43.66, 31) * mm, "end": v(38.66, 31) * mm});
            skLineSegment(sketch, "E340", {"start": v(38.66, 31) * mm, "end": v(38.66, 29) * mm});
            skLineSegment(sketch, "E341", {"start": v(38.66, 29) * mm, "end": v(43.66, 29) * mm});
            skLineSegment(sketch, "E342", {"start": v(43.66, 29) * mm, "end": v(43.66, 24) * mm});
            skLineSegment(sketch, "E343", {"start": v(43.66, 24) * mm, "end": v(45.66, 24) * mm});
            skLineSegment(sketch, "E344", {"start": v(45.66, 24) * mm, "end": v(45.66, 29) * mm});
            skLineSegment(sketch, "E345", {"start": v(45.66, 29) * mm, "end": v(50.66, 29) * mm});
            skLineSegment(sketch, "E346", {"start": v(50.66, 29) * mm, "end": v(50.66, 31) * mm});
            skLineSegment(sketch, "E347", {"start": v(50.66, 31) * mm, "end": v(45.66, 31) * mm});
            skLineSegment(sketch, "E348", {"start": v(45.66, 31) * mm, "end": v(45.66, 36) * mm});
            skLineSegment(sketch, "E349", {"start": v(45.66, 36) * mm, "end": v(43.66, 36) * mm});
            skLineSegment(sketch, "E350.bottom", {"start": v(4, 51) * mm, "end": v(16, 51) * mm});
            skLineSegment(sketch, "E350.top", {"start": v(4, 49) * mm, "end": v(16, 49) * mm});
            skLineSegment(sketch, "E350.left", {"start": v(4, 51) * mm, "end": v(4, 49) * mm});
            skLineSegment(sketch, "E350.right", {"start": v(16, 51) * mm, "end": v(16, 49) * mm});
            skLineSegment(sketch, "E351.bottom", {"start": v(33.33, 61) * mm, "end": v(21.33, 61) * mm});
            skLineSegment(sketch, "E351.top", {"start": v(21.33, 59) * mm, "end": v(33.33, 59) * mm});
            skLineSegment(sketch, "E351.left", {"start": v(21.33, 61) * mm, "end": v(21.33, 59) * mm});
            skLineSegment(sketch, "E351.right", {"start": v(33.33, 61) * mm, "end": v(33.33, 59) * mm});
            skLineSegment(sketch, "E352.bottom", {"start": v(38.66, 51) * mm, "end": v(50.66, 51) * mm});
            skLineSegment(sketch, "E352.top", {"start": v(38.66, 49) * mm, "end": v(50.66, 49) * mm});
            skLineSegment(sketch, "E352.left", {"start": v(38.66, 51) * mm, "end": v(38.66, 49) * mm});
            skLineSegment(sketch, "E352.right", {"start": v(50.66, 51) * mm, "end": v(50.66, 49) * mm});
            skLineSegment(sketch, "E353.bottom", {"start": v(56, 61) * mm, "end": v(68, 61) * mm});
            skLineSegment(sketch, "E353.top", {"start": v(56, 59) * mm, "end": v(68, 59) * mm});
            skLineSegment(sketch, "E353.left", {"start": v(56, 61) * mm, "end": v(56, 59) * mm});
            skLineSegment(sketch, "E353.right", {"start": v(68, 61) * mm, "end": v(68, 59) * mm});
            skLineSegment(sketch, "E354.bottom", {"start": v(73.32, 51) * mm, "end": v(85.32, 51) * mm});
            skLineSegment(sketch, "E354.top", {"start": v(73.32, 49) * mm, "end": v(85.32, 49) * mm});
            skLineSegment(sketch, "E354.left", {"start": v(73.32, 51) * mm, "end": v(73.32, 49) * mm});
            skLineSegment(sketch, "E354.right", {"start": v(85.32, 51) * mm, "end": v(85.32, 49) * mm});
            skLineSegment(sketch, "E355", {"start": v(9, 76) * mm, "end": v(9, 71) * mm});
            skLineSegment(sketch, "E356", {"start": v(9, 71) * mm, "end": v(4, 71) * mm});
            skLineSegment(sketch, "E357", {"start": v(4, 71) * mm, "end": v(4, 69) * mm});
            skLineSegment(sketch, "E358", {"start": v(4, 69) * mm, "end": v(9, 69) * mm});
            skLineSegment(sketch, "E359", {"start": v(9, 69) * mm, "end": v(9, 64) * mm});
            skLineSegment(sketch, "E360", {"start": v(9, 64) * mm, "end": v(11, 64) * mm});
            skLineSegment(sketch, "E361", {"start": v(11, 64) * mm, "end": v(11, 69) * mm});
            skLineSegment(sketch, "E362", {"start": v(11, 69) * mm, "end": v(16, 69) * mm});
            skLineSegment(sketch, "E363", {"start": v(16, 69) * mm, "end": v(16, 71) * mm});
            skLineSegment(sketch, "E364", {"start": v(16, 71) * mm, "end": v(11, 71) * mm});
            skLineSegment(sketch, "E365", {"start": v(11, 71) * mm, "end": v(11, 76) * mm});
            skLineSegment(sketch, "E366", {"start": v(11, 76) * mm, "end": v(9, 76) * mm});
            skLineSegment(sketch, "E367", {"start": v(26.33, 86) * mm, "end": v(26.33, 81) * mm});
            skLineSegment(sketch, "E368", {"start": v(26.33, 81) * mm, "end": v(21.33, 81) * mm});
            skLineSegment(sketch, "E369", {"start": v(21.33, 81) * mm, "end": v(21.33, 79) * mm});
            skLineSegment(sketch, "E370", {"start": v(21.33, 79) * mm, "end": v(26.33, 79) * mm});
            skLineSegment(sketch, "E371", {"start": v(26.33, 79) * mm, "end": v(26.33, 74) * mm});
            skLineSegment(sketch, "E372", {"start": v(26.33, 74) * mm, "end": v(28.33, 74) * mm});
            skLineSegment(sketch, "E373", {"start": v(28.33, 74) * mm, "end": v(28.33, 79) * mm});
            skLineSegment(sketch, "E374", {"start": v(28.33, 79) * mm, "end": v(33.33, 79) * mm});
            skLineSegment(sketch, "E375", {"start": v(33.33, 79) * mm, "end": v(33.33, 81) * mm});
            skLineSegment(sketch, "E376", {"start": v(33.33, 81) * mm, "end": v(28.33, 81) * mm});
            skLineSegment(sketch, "E377", {"start": v(28.33, 81) * mm, "end": v(28.33, 86) * mm});
            skLineSegment(sketch, "E378", {"start": v(28.33, 86) * mm, "end": v(26.33, 86) * mm});
            skLineSegment(sketch, "E379", {"start": v(78.32, 76) * mm, "end": v(78.32, 71) * mm});
            skLineSegment(sketch, "E380", {"start": v(78.32, 71) * mm, "end": v(73.32, 71) * mm});
            skLineSegment(sketch, "E381", {"start": v(73.32, 71) * mm, "end": v(73.32, 69) * mm});
            skLineSegment(sketch, "E382", {"start": v(73.32, 69) * mm, "end": v(78.32, 69) * mm});
            skLineSegment(sketch, "E383", {"start": v(78.32, 69) * mm, "end": v(78.32, 64) * mm});
            skLineSegment(sketch, "E384", {"start": v(78.32, 64) * mm, "end": v(80.32, 64) * mm});
            skLineSegment(sketch, "E385", {"start": v(80.32, 64) * mm, "end": v(80.32, 69) * mm});
            skLineSegment(sketch, "E386", {"start": v(80.32, 69) * mm, "end": v(85.32, 69) * mm});
            skLineSegment(sketch, "E387", {"start": v(85.32, 69) * mm, "end": v(85.32, 71) * mm});
            skLineSegment(sketch, "E388", {"start": v(85.32, 71) * mm, "end": v(80.32, 71) * mm});
            skLineSegment(sketch, "E389", {"start": v(80.32, 71) * mm, "end": v(80.32, 76) * mm});
            skLineSegment(sketch, "E390", {"start": v(80.32, 76) * mm, "end": v(78.32, 76) * mm});
            skLineSegment(sketch, "E391", {"start": v(61, 86) * mm, "end": v(61, 81) * mm});
            skLineSegment(sketch, "E392", {"start": v(61, 81) * mm, "end": v(56, 81) * mm});
            skLineSegment(sketch, "E393", {"start": v(56, 81) * mm, "end": v(56, 79) * mm});
            skLineSegment(sketch, "E394", {"start": v(56, 79) * mm, "end": v(61, 79) * mm});
            skLineSegment(sketch, "E395", {"start": v(61, 79) * mm, "end": v(61, 74) * mm});
            skLineSegment(sketch, "E396", {"start": v(61, 74) * mm, "end": v(63, 74) * mm});
            skLineSegment(sketch, "E397", {"start": v(63, 74) * mm, "end": v(63, 79) * mm});
            skLineSegment(sketch, "E398", {"start": v(63, 79) * mm, "end": v(68, 79) * mm});
            skLineSegment(sketch, "E399", {"start": v(68, 79) * mm, "end": v(68, 81) * mm});
            skLineSegment(sketch, "E400", {"start": v(68, 81) * mm, "end": v(63, 81) * mm});
            skLineSegment(sketch, "E401", {"start": v(63, 81) * mm, "end": v(63, 86) * mm});
            skLineSegment(sketch, "E402", {"start": v(63, 86) * mm, "end": v(61, 86) * mm});
            skLineSegment(sketch, "E403", {"start": v(43.66, 76) * mm, "end": v(43.66, 71) * mm});
            skLineSegment(sketch, "E404", {"start": v(43.66, 71) * mm, "end": v(38.66, 71) * mm});
            skLineSegment(sketch, "E405", {"start": v(38.66, 71) * mm, "end": v(38.66, 69) * mm});
            skLineSegment(sketch, "E406", {"start": v(38.66, 69) * mm, "end": v(43.66, 69) * mm});
            skLineSegment(sketch, "E407", {"start": v(43.66, 69) * mm, "end": v(43.66, 64) * mm});
            skLineSegment(sketch, "E408", {"start": v(43.66, 64) * mm, "end": v(45.66, 64) * mm});
            skLineSegment(sketch, "E409", {"start": v(45.66, 64) * mm, "end": v(45.66, 69) * mm});
            skLineSegment(sketch, "E410", {"start": v(45.66, 69) * mm, "end": v(50.66, 69) * mm});
            skLineSegment(sketch, "E411", {"start": v(50.66, 69) * mm, "end": v(50.66, 71) * mm});
            skLineSegment(sketch, "E412", {"start": v(50.66, 71) * mm, "end": v(45.66, 71) * mm});
            skLineSegment(sketch, "E413", {"start": v(45.66, 71) * mm, "end": v(45.66, 76) * mm});
            skLineSegment(sketch, "E414", {"start": v(45.66, 76) * mm, "end": v(43.66, 76) * mm});
            skLineSegment(sketch, "E415.bottom", {"start": v(4, 91) * mm, "end": v(16, 91) * mm});
            skLineSegment(sketch, "E415.top", {"start": v(4, 89) * mm, "end": v(16, 89) * mm});
            skLineSegment(sketch, "E415.left", {"start": v(4, 91) * mm, "end": v(4, 89) * mm});
            skLineSegment(sketch, "E415.right", {"start": v(16, 91) * mm, "end": v(16, 89) * mm});
            skLineSegment(sketch, "E416.bottom", {"start": v(33.33, 101) * mm, "end": v(21.33, 101) * mm});
            skLineSegment(sketch, "E416.top", {"start": v(21.33, 99) * mm, "end": v(33.33, 99) * mm});
            skLineSegment(sketch, "E416.left", {"start": v(21.33, 101) * mm, "end": v(21.33, 99) * mm});
            skLineSegment(sketch, "E416.right", {"start": v(33.33, 101) * mm, "end": v(33.33, 99) * mm});
            skLineSegment(sketch, "E417.bottom", {"start": v(38.66, 91) * mm, "end": v(50.66, 91) * mm});
            skLineSegment(sketch, "E417.top", {"start": v(38.66, 89) * mm, "end": v(50.66, 89) * mm});
            skLineSegment(sketch, "E417.left", {"start": v(38.66, 91) * mm, "end": v(38.66, 89) * mm});
            skLineSegment(sketch, "E417.right", {"start": v(50.66, 91) * mm, "end": v(50.66, 89) * mm});
            skLineSegment(sketch, "E418.bottom", {"start": v(56, 101) * mm, "end": v(68, 101) * mm});
            skLineSegment(sketch, "E418.top", {"start": v(56, 99) * mm, "end": v(68, 99) * mm});
            skLineSegment(sketch, "E418.left", {"start": v(56, 101) * mm, "end": v(56, 99) * mm});
            skLineSegment(sketch, "E418.right", {"start": v(68, 101) * mm, "end": v(68, 99) * mm});
            skLineSegment(sketch, "E419.bottom", {"start": v(73.32, 91) * mm, "end": v(85.32, 91) * mm});
            skLineSegment(sketch, "E419.top", {"start": v(73.32, 89) * mm, "end": v(85.32, 89) * mm});
            skLineSegment(sketch, "E419.left", {"start": v(73.32, 91) * mm, "end": v(73.32, 89) * mm});
            skLineSegment(sketch, "E419.right", {"start": v(85.32, 91) * mm, "end": v(85.32, 89) * mm});
            skLineSegment(sketch, "E420", {"start": v(9, 116) * mm, "end": v(9, 111) * mm});
            skLineSegment(sketch, "E421", {"start": v(9, 111) * mm, "end": v(4, 111) * mm});
            skLineSegment(sketch, "E422", {"start": v(4, 111) * mm, "end": v(4, 109) * mm});
            skLineSegment(sketch, "E423", {"start": v(4, 109) * mm, "end": v(9, 109) * mm});
            skLineSegment(sketch, "E424", {"start": v(9, 109) * mm, "end": v(9, 104) * mm});
            skLineSegment(sketch, "E425", {"start": v(9, 104) * mm, "end": v(11, 104) * mm});
            skLineSegment(sketch, "E426", {"start": v(11, 104) * mm, "end": v(11, 109) * mm});
            skLineSegment(sketch, "E427", {"start": v(11, 109) * mm, "end": v(16, 109) * mm});
            skLineSegment(sketch, "E428", {"start": v(16, 109) * mm, "end": v(16, 111) * mm});
            skLineSegment(sketch, "E429", {"start": v(16, 111) * mm, "end": v(11, 111) * mm});
            skLineSegment(sketch, "E430", {"start": v(11, 111) * mm, "end": v(11, 116) * mm});
            skLineSegment(sketch, "E431", {"start": v(11, 116) * mm, "end": v(9, 116) * mm});
            skLineSegment(sketch, "E432", {"start": v(26.33, 126) * mm, "end": v(26.33, 121) * mm});
            skLineSegment(sketch, "E433", {"start": v(26.33, 121) * mm, "end": v(21.33, 121) * mm});
            skLineSegment(sketch, "E434", {"start": v(21.33, 121) * mm, "end": v(21.33, 119) * mm});
            skLineSegment(sketch, "E435", {"start": v(21.33, 119) * mm, "end": v(26.33, 119) * mm});
            skLineSegment(sketch, "E436", {"start": v(26.33, 119) * mm, "end": v(26.33, 114) * mm});
            skLineSegment(sketch, "E437", {"start": v(26.33, 114) * mm, "end": v(28.33, 114) * mm});
            skLineSegment(sketch, "E438", {"start": v(28.33, 114) * mm, "end": v(28.33, 119) * mm});
            skLineSegment(sketch, "E439", {"start": v(28.33, 119) * mm, "end": v(33.33, 119) * mm});
            skLineSegment(sketch, "E440", {"start": v(33.33, 119) * mm, "end": v(33.33, 121) * mm});
            skLineSegment(sketch, "E441", {"start": v(33.33, 121) * mm, "end": v(28.33, 121) * mm});
            skLineSegment(sketch, "E442", {"start": v(28.33, 121) * mm, "end": v(28.33, 126) * mm});
            skLineSegment(sketch, "E443", {"start": v(28.33, 126) * mm, "end": v(26.33, 126) * mm});
            skLineSegment(sketch, "E444", {"start": v(78.32, 116) * mm, "end": v(78.32, 111) * mm});
            skLineSegment(sketch, "E445", {"start": v(78.32, 111) * mm, "end": v(73.32, 111) * mm});
            skLineSegment(sketch, "E446", {"start": v(73.32, 111) * mm, "end": v(73.32, 109) * mm});
            skLineSegment(sketch, "E447", {"start": v(73.32, 109) * mm, "end": v(78.32, 109) * mm});
            skLineSegment(sketch, "E448", {"start": v(78.32, 109) * mm, "end": v(78.32, 104) * mm});
            skLineSegment(sketch, "E449", {"start": v(78.32, 104) * mm, "end": v(80.32, 104) * mm});
            skLineSegment(sketch, "E450", {"start": v(80.32, 104) * mm, "end": v(80.32, 109) * mm});
            skLineSegment(sketch, "E451", {"start": v(80.32, 109) * mm, "end": v(85.32, 109) * mm});
            skLineSegment(sketch, "E452", {"start": v(85.32, 109) * mm, "end": v(85.32, 111) * mm});
            skLineSegment(sketch, "E453", {"start": v(85.32, 111) * mm, "end": v(80.32, 111) * mm});
            skLineSegment(sketch, "E454", {"start": v(80.32, 111) * mm, "end": v(80.32, 116) * mm});
            skLineSegment(sketch, "E455", {"start": v(80.32, 116) * mm, "end": v(78.32, 116) * mm});
            skLineSegment(sketch, "E456", {"start": v(60.99, 126) * mm, "end": v(60.99, 121) * mm});
            skLineSegment(sketch, "E457", {"start": v(60.99, 121) * mm, "end": v(56, 121) * mm});
            skLineSegment(sketch, "E458", {"start": v(56, 121) * mm, "end": v(56, 119) * mm});
            skLineSegment(sketch, "E459", {"start": v(56, 119) * mm, "end": v(60.99, 119) * mm});
            skLineSegment(sketch, "E460", {"start": v(60.99, 119) * mm, "end": v(60.99, 114) * mm});
            skLineSegment(sketch, "E461", {"start": v(60.99, 114) * mm, "end": v(63, 114) * mm});
            skLineSegment(sketch, "E462", {"start": v(63, 114) * mm, "end": v(63, 119) * mm});
            skLineSegment(sketch, "E463", {"start": v(63, 119) * mm, "end": v(68, 119) * mm});
            skLineSegment(sketch, "E464", {"start": v(68, 119) * mm, "end": v(68, 121) * mm});
            skLineSegment(sketch, "E465", {"start": v(68, 121) * mm, "end": v(63, 121) * mm});
            skLineSegment(sketch, "E466", {"start": v(63, 121) * mm, "end": v(63, 126) * mm});
            skLineSegment(sketch, "E467", {"start": v(63, 126) * mm, "end": v(60.99, 126) * mm});
            skLineSegment(sketch, "E468", {"start": v(43.66, 116) * mm, "end": v(43.66, 111) * mm});
            skLineSegment(sketch, "E469", {"start": v(43.66, 111) * mm, "end": v(38.66, 111) * mm});
            skLineSegment(sketch, "E470", {"start": v(38.66, 111) * mm, "end": v(38.66, 109) * mm});
            skLineSegment(sketch, "E471", {"start": v(38.66, 109) * mm, "end": v(43.66, 109) * mm});
            skLineSegment(sketch, "E472", {"start": v(43.66, 109) * mm, "end": v(43.66, 104) * mm});
            skLineSegment(sketch, "E473", {"start": v(43.66, 104) * mm, "end": v(45.66, 104) * mm});
            skLineSegment(sketch, "E474", {"start": v(45.66, 104) * mm, "end": v(45.66, 109) * mm});
            skLineSegment(sketch, "E475", {"start": v(45.66, 109) * mm, "end": v(50.66, 109) * mm});
            skLineSegment(sketch, "E476", {"start": v(50.66, 109) * mm, "end": v(50.66, 111) * mm});
            skLineSegment(sketch, "E477", {"start": v(50.66, 111) * mm, "end": v(45.66, 111) * mm});
            skLineSegment(sketch, "E478", {"start": v(45.66, 111) * mm, "end": v(45.66, 116) * mm});
            skLineSegment(sketch, "E479", {"start": v(45.66, 116) * mm, "end": v(43.66, 116) * mm});
            skLineSegment(sketch, "E480.bottom", {"start": v(4, 131) * mm, "end": v(16, 131) * mm});
            skLineSegment(sketch, "E480.top", {"start": v(4, 129) * mm, "end": v(16, 129) * mm});
            skLineSegment(sketch, "E480.left", {"start": v(4, 131) * mm, "end": v(4, 129) * mm});
            skLineSegment(sketch, "E480.right", {"start": v(16, 131) * mm, "end": v(16, 129) * mm});
            skLineSegment(sketch, "E481.bottom", {"start": v(33.33, 141) * mm, "end": v(21.33, 141) * mm});
            skLineSegment(sketch, "E481.top", {"start": v(21.33, 139) * mm, "end": v(33.33, 139) * mm});
            skLineSegment(sketch, "E481.left", {"start": v(21.33, 141) * mm, "end": v(21.33, 139) * mm});
            skLineSegment(sketch, "E481.right", {"start": v(33.33, 141) * mm, "end": v(33.33, 139) * mm});
            skLineSegment(sketch, "E482.bottom", {"start": v(38.66, 131) * mm, "end": v(50.66, 131) * mm});
            skLineSegment(sketch, "E482.top", {"start": v(38.66, 129) * mm, "end": v(50.66, 129) * mm});
            skLineSegment(sketch, "E482.left", {"start": v(38.66, 131) * mm, "end": v(38.66, 129) * mm});
            skLineSegment(sketch, "E482.right", {"start": v(50.66, 131) * mm, "end": v(50.66, 129) * mm});
            skLineSegment(sketch, "E483.bottom", {"start": v(56, 141) * mm, "end": v(68, 141) * mm});
            skLineSegment(sketch, "E483.top", {"start": v(56, 139) * mm, "end": v(68, 139) * mm});
            skLineSegment(sketch, "E483.left", {"start": v(56, 141) * mm, "end": v(56, 139) * mm});
            skLineSegment(sketch, "E483.right", {"start": v(68, 141) * mm, "end": v(68, 139) * mm});
            skLineSegment(sketch, "E484.bottom", {"start": v(73.32, 131) * mm, "end": v(85.32, 131) * mm});
            skLineSegment(sketch, "E484.top", {"start": v(73.32, 129) * mm, "end": v(85.32, 129) * mm});
            skLineSegment(sketch, "E484.left", {"start": v(73.32, 131) * mm, "end": v(73.32, 129) * mm});
            skLineSegment(sketch, "E484.right", {"start": v(85.32, 131) * mm, "end": v(85.32, 129) * mm});
            skLineSegment(sketch, "E485.bottom", {"start": v(4, 11) * mm, "end": v(16, 11) * mm});
            skLineSegment(sketch, "E485.top", {"start": v(4, 9) * mm, "end": v(16, 9) * mm});
            skLineSegment(sketch, "E485.left", {"start": v(4, 11) * mm, "end": v(4, 9) * mm});
            skLineSegment(sketch, "E485.right", {"start": v(16, 11) * mm, "end": v(16, 9) * mm});
            skLineSegment(sketch, "E486.bottom", {"start": v(33.33, 21) * mm, "end": v(21.33, 21) * mm});
            skLineSegment(sketch, "E486.top", {"start": v(21.33, 19) * mm, "end": v(33.33, 19) * mm});
            skLineSegment(sketch, "E486.left", {"start": v(21.33, 21) * mm, "end": v(21.33, 19) * mm});
            skLineSegment(sketch, "E486.right", {"start": v(33.33, 21) * mm, "end": v(33.33, 19) * mm});
            skLineSegment(sketch, "E487.bottom", {"start": v(38.66, 11) * mm, "end": v(50.66, 11) * mm});
            skLineSegment(sketch, "E487.top", {"start": v(38.66, 9) * mm, "end": v(50.66, 9) * mm});
            skLineSegment(sketch, "E487.left", {"start": v(38.66, 11) * mm, "end": v(38.66, 9) * mm});
            skLineSegment(sketch, "E487.right", {"start": v(50.66, 11) * mm, "end": v(50.66, 9) * mm});
            skLineSegment(sketch, "E488.bottom", {"start": v(56, 21) * mm, "end": v(68, 21) * mm});
            skLineSegment(sketch, "E488.top", {"start": v(56, 19) * mm, "end": v(68, 19) * mm});
            skLineSegment(sketch, "E488.left", {"start": v(56, 21) * mm, "end": v(56, 19) * mm});
            skLineSegment(sketch, "E488.right", {"start": v(68, 21) * mm, "end": v(68, 19) * mm});
            skLineSegment(sketch, "E489.bottom", {"start": v(73.32, 11) * mm, "end": v(85.32, 11) * mm});
            skLineSegment(sketch, "E489.top", {"start": v(73.32, 9) * mm, "end": v(85.32, 9) * mm});
            skLineSegment(sketch, "E489.left", {"start": v(73.32, 11) * mm, "end": v(73.32, 9) * mm});
            skLineSegment(sketch, "E489.right", {"start": v(85.32, 11) * mm, "end": v(85.32, 9) * mm});
            skSolve(sketch);
        }
        {
            var Q0;
            Q0=qSketchRegion(id+"F4",true);
            extrude(context, id + "F5", {"entities" : qUnion([Q0]), "operationType" : NewBodyOperationType.REMOVE, "oppositeDirection" : true, "depth" : 2 * mm, "offsetDistance" : 25 * mm});
        }
    });
